# Revit family: Haworth_Worksurface_SupportPanel
name_source: partatom
category: Furniture Systems
revit_build: Autodesk Revit 2018 (Build: 20170223_1515(x64)
units: mm (PartAtom-declared; Revit-internal decimal feet)

## family parameters
Always vertical = Yes
Cut with Voids When Loaded = No
OmniClass Number = 23.40.70.14.64.21
OmniClass Title = Systems Furniture
Part Type = Normal
Room Calculation Point = No
Round Connector Dimension = Use Diameter
Shared = No
Work Plane-Based = No

## types (3) — shared parameters
Actual Top Thickness = 1 3/16"
Assembly Code = E2020200
Description = Haworth - Worksurface Support Panel
Manufacturer = Haworth
Max. Depth = 36"
Max. Height = 32"
Min. Depth = 12"
Min. Height = 26"
Min/Max Height = 26-32 in.
Model = Haworth - Worksurface Support Panel
Revision Number = 3
Size = Verify Final Dim. w/ Haworth
Standard Depths = 12, 18, 24, 30 in.
Support Thickness = 6"
Sustainability Info = http://www.haworth.com
URL = www.haworth.com
URL - Product = http://www.haworth.com
Warranty = http://www.haworth.com
Worksurface Thickness = 1 3/16"

## per-type parameters (varying)
| type | Actual Depth | Actual Height | Depth | Support Finish | Support Height | Worksurface Height |
| 12d | 12" | 21 9/16" | 12" | Haworth _ Laminate _ Linen H-WL | 20 3/8" | 21 9/16" |
| 24d | 24" | 26" | 24" | Haworth _ Wood _ White Oak | 24 13/16" | 18" |
| 36d | 36" | 29 49/256" | 36" | Haworth _ Laminate _ Linen H-WL | 28 1/256" | 29 49/256" |

## geometry (parser evidence)
native form markers: Sweep x3
no freeform markers — native parametric forms only
